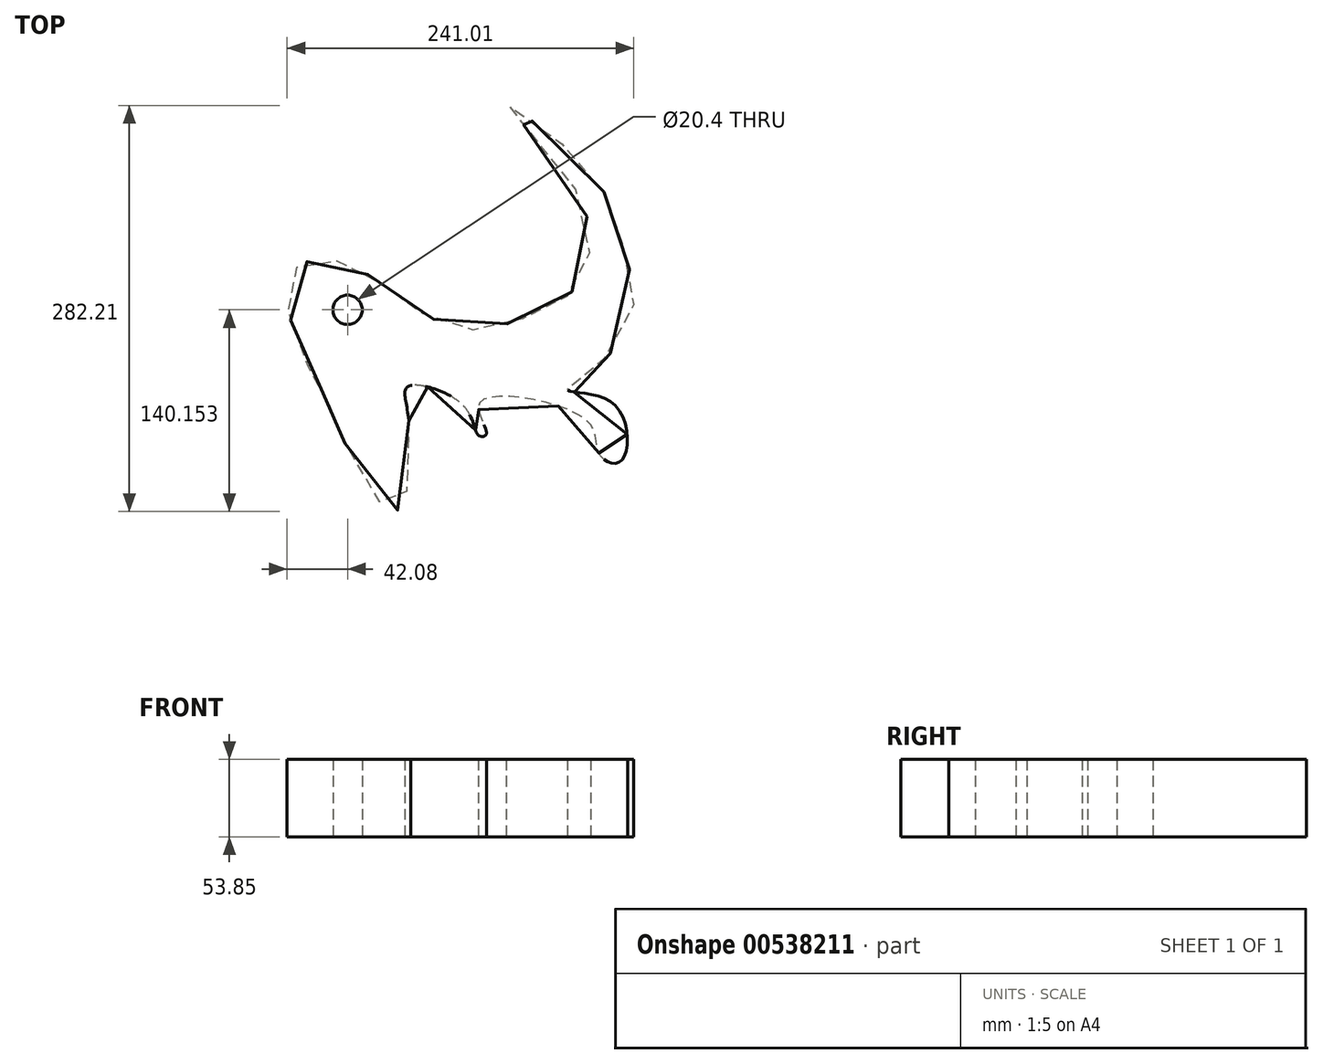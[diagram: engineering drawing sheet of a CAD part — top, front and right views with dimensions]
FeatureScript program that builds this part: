
annotation { "Feature Type Name" : "Feature", "Feature Type Description" : "" }
export const myFeature = defineFeature(function(context is Context, id is Id, definition is map)
    precondition{}
    {
        {
            var Q0;
            Q0=qCreatedBy(makeId("Top.planeOp"),FACE);
            var sketch = newSketch(context, id + "F0", { "sketchPlane" : qUnion([Q0])});
            skFitSpline(sketch, "E0", {"points": [v(0, 0) * mm, v(-10.52, -63.19) * mm, v(-51.63, 0) * mm, v(-56.36, 12.83) * mm, v(-76.7, 52) * mm, v(-81.02, 103.02) * mm, v(-53.43, 111.77) * mm, v(-16.08, 92.87) * mm, v(33.76, 64.2) * mm, v(83.15, 72.48) * mm, v(119.4, 97.33) * mm, v(114.4, 163.63) * mm, v(67.77, 218.96) * mm, v(121.1, 178.6) * mm, v(147.31, 125.85) * mm, v(149.61, 57.99) * mm, v(110.27, 21.56) * mm, v(142, 11.82) * mm, v(147.2, -28.27) * mm, v(132.2, -23.22) * mm, v(123.63, 0) * mm, v(49.27, 12.45) * mm, v(53.85, -9.05) * mm, v(48.88, -10.62) * mm, v(38.56, 9.53) * mm, v(0, 23.96) * mm, v(0, 0) * mm]});
            skSolve(sketch);
        }
        {
            var Q0;
            Q0 = qSketchRegion(id + "F0", true);
            extrude(context, id + "F1", {"entities" : qUnion([Q0]), "depth" : 53.85 * mm, "offsetDistance" : 25.4 * mm});
        }
        {
            var Q0;
            Q0=qCreatedBy(makeId("Top.planeOp"),FACE);
            var sketch = newSketch(context, id + "F2", { "sketchPlane" : qUnion([Q0])});
            skCircle(sketch, "E1", {"center": v(-42.65, 76.96) * mm, "radius": 10.2 * mm});
            skSolve(sketch);
        }
        {
            var Q0;
            Q0 = qSketchRegion(id + "F2", true);
            extrude(context, id + "F3", {"entities" : qUnion([Q0]), "operationType" : NewBodyOperationType.REMOVE, "depth" : 64.26 * mm, "offsetDistance" : 25.4 * mm});
        }
    });
